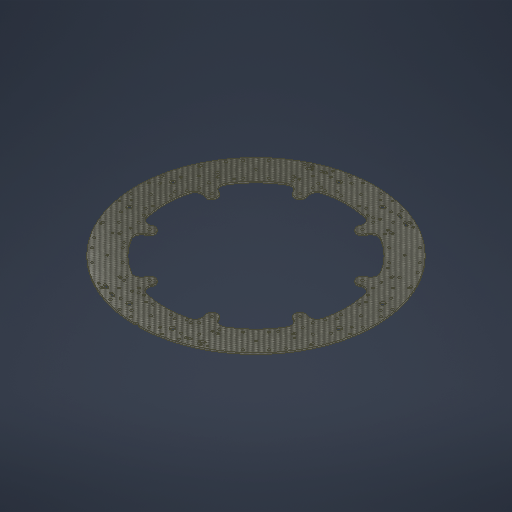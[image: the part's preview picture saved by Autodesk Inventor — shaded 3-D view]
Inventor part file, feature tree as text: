
AUTODESK INVENTOR PART (.ipt)
format: ipt  version: 2025 (Build 290162010, 162A)  size: 765,952 bytes
history: native  units: mm
features: extrude x1, sketch x1
ambient origin geometry x8: Origin, YZ Plane, XZ Plane, XY Plane, X Axis, Y Axis, Z Axis, Center Point
bodies: Solid1 (feature_tree)
feature tree (2):
  extrude  "Extrusion1"  Depth=2.0mm
  sketch  "Sketch1"  dims[d0=2.0mm d1=0.0mm d2=2.0mm]
